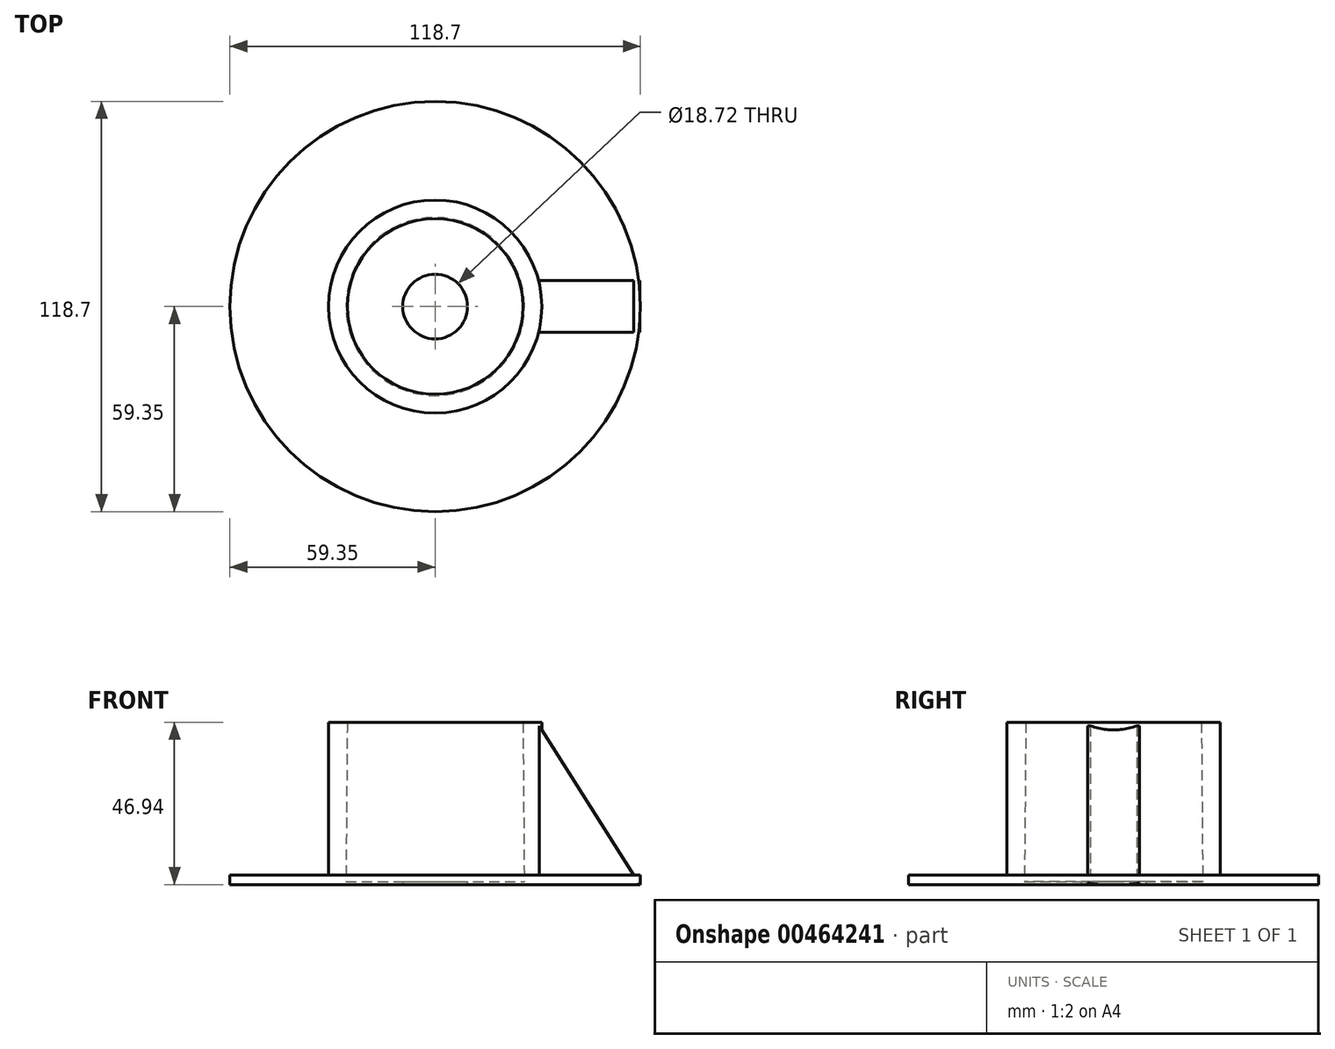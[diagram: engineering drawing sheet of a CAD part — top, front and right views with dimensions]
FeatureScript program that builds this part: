
annotation { "Feature Type Name" : "Feature", "Feature Type Description" : "" }
export const myFeature = defineFeature(function(context is Context, id is Id, definition is map)
    precondition{}
    {
        {
            var Q0;
            Q0=qCreatedBy(makeId("Front.planeOp"),FACE);
            var sketch = newSketch(context, id + "F0", { "sketchPlane" : qUnion([Q0])});
            skLineSegment(sketch, "E0", {"start": v(59.35, 0) * mm, "end": v(9.36, 0) * mm});
            skLineSegment(sketch, "E1", {"start": v(25.4, 46.94) * mm, "end": v(30.84, 46.94) * mm});
            skLineSegment(sketch, "E2", {"start": v(30.84, 46.94) * mm, "end": v(30.84, 2.72) * mm});
            skLineSegment(sketch, "E3", {"start": v(30.84, 2.72) * mm, "end": v(59.35, 2.72) * mm});
            skLineSegment(sketch, "E4", {"start": v(59.35, 2.72) * mm, "end": v(59.35, 0) * mm});
            skLineSegment(sketch, "E5", {"start": v(9.36, 0) * mm, "end": v(9.36, 0.84) * mm});
            skLineSegment(sketch, "E6", {"start": v(9.36, 0.84) * mm, "end": v(25.79, 0.84) * mm});
            skLineSegment(sketch, "E7", {"start": v(25.79, 0.84) * mm, "end": v(25.4, 46.94) * mm});
            skSolve(sketch);
        }
        {
            var Q0;
            Q0=qCreatedBy(makeId("Front.planeOp"),FACE);
            var sketch = newSketch(context, id + "F1", { "sketchPlane" : qUnion([Q0])});
            skLineSegment(sketch, "E8", {"start": v(0, 0) * mm, "end": v(0, 74.44) * mm});
            skSolve(sketch);
        }
        {
            var Q0;
            Q0 = qSketchRegion(id + "F0", true);
            var Q1;
            Q1=sQuery(id+"F1.wireOp",EDGE,"E8");
            revolve(context, id + "F2", {"entities" : qUnion([Q0]), "axis" : qUnion([Q1]), "revolveType" : RevolveType.FULL});
        }
        {
            var Q0;
            Q0=qCreatedBy(makeId("Front.planeOp"),FACE);
            var sketch = newSketch(context, id + "F3", { "sketchPlane" : qUnion([Q0])});
            skLineSegment(sketch, "E9", {"start": v(30.1, 45.93) * mm, "end": v(30.1, 0) * mm});
            skLineSegment(sketch, "E10", {"start": v(30.1, 0) * mm, "end": v(59.18, 0) * mm});
            skLineSegment(sketch, "E11", {"start": v(59.18, 0) * mm, "end": v(30.1, 45.93) * mm});
            skSolve(sketch);
        }
        {
            var Q0;
            Q0 = qSketchRegion(id + "F3", true);
            extrude(context, id + "F4", {"entities" : qUnion([Q0]), "operationType" : NewBodyOperationType.ADD, "endBound" : BoundingType.SYMMETRIC, "depth" : 15 * mm});
        }
    });
